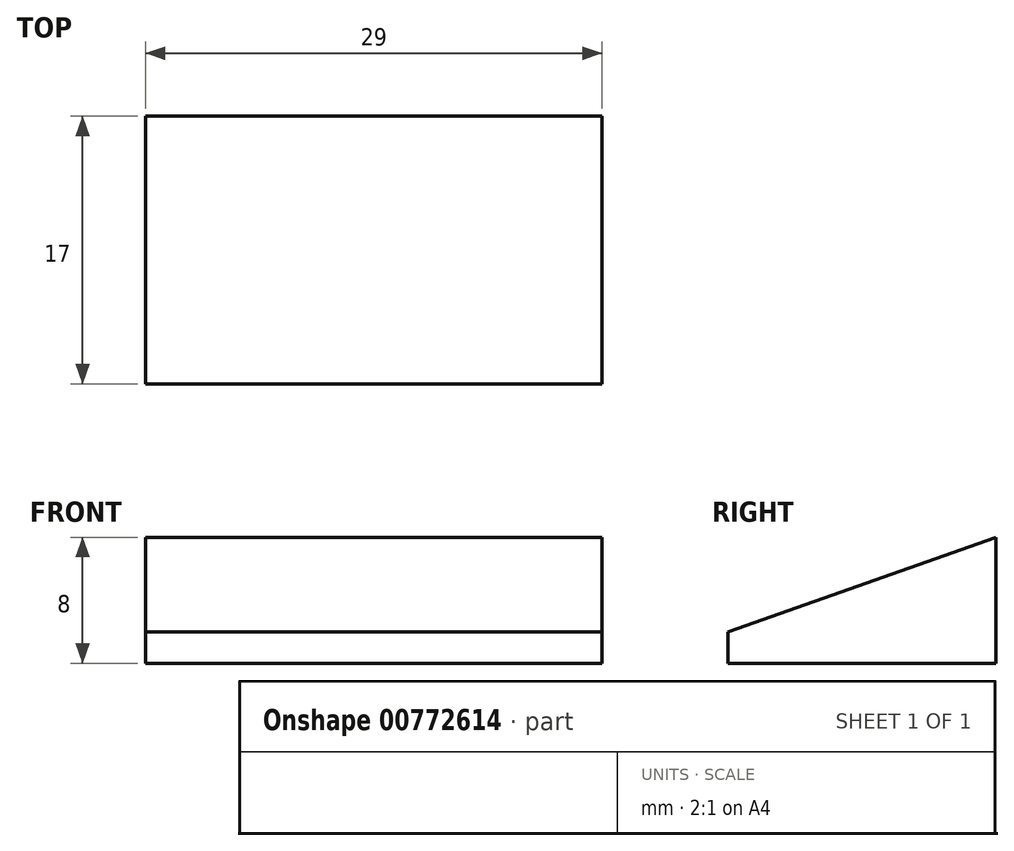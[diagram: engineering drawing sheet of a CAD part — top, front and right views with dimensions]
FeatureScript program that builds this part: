
annotation { "Feature Type Name" : "Feature", "Feature Type Description" : "" }
export const myFeature = defineFeature(function(context is Context, id is Id, definition is map)
    precondition{}
    {
        {
            var Q0;
            Q0=qCreatedBy(makeId("Top.planeOp"),FACE);
            var sketch = newSketch(context, id + "F0", { "sketchPlane" : qUnion([Q0])});
            skLineSegment(sketch, "E0.bottom", {"start": v(14.5, 8.5) * mm, "end": v(-14.5, 8.5) * mm});
            skLineSegment(sketch, "E0.top", {"start": v(14.5, -8.5) * mm, "end": v(-14.5, -8.5) * mm});
            skLineSegment(sketch, "E0.left", {"start": v(14.5, 8.5) * mm, "end": v(14.5, -8.5) * mm});
            skLineSegment(sketch, "E0.right", {"start": v(-14.5, 8.5) * mm, "end": v(-14.5, -8.5) * mm});
            skPoint(sketch, "E0.middle", {"position": v(0, 0) * mm});
            skSolve(sketch);
        }
        {
            var Q0;
            Q0 = qSketchRegion(id + "F0", true);
            extrude(context, id + "F1", {"entities" : qUnion([Q0]), "depth" : 8 * mm, "offsetDistance" : 25.4 * mm});
        }
        {
            var Q0;
            Q0=makeQuery(id+"F1.opExtrude","SWEPT_FACE",FACE,{"disambiguationData":[OSD([sQuery(id+"F0.wireOp",EDGE,"E0.left")])]});
            var sketch = newSketch(context, id + "F2", { "sketchPlane" : qUnion([Q0])});
            skLineSegment(sketch, "E1", {"start": v(8.5, 8) * mm, "end": v(-8.5, 8) * mm});
            skLineSegment(sketch, "E2", {"start": v(-8.5, 8) * mm, "end": v(-8.5, 2) * mm});
            skLineSegment(sketch, "E3", {"start": v(-8.5, 2) * mm, "end": v(8.5, 8) * mm});
            skSolve(sketch);
        }
        {
            var Q0;
            Q0 = qSketchRegion(id + "F2", true);
            extrude(context, id + "F3", {"entities" : qUnion([Q0]), "operationType" : NewBodyOperationType.REMOVE, "oppositeDirection" : true, "depth" : 1143 * mm, "offsetDistance" : 25.4 * mm});
        }
    });
